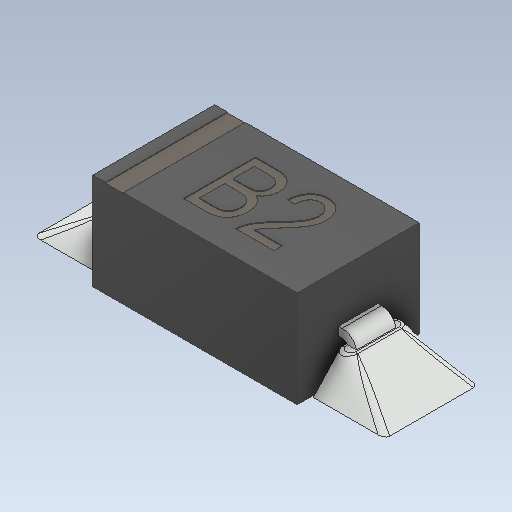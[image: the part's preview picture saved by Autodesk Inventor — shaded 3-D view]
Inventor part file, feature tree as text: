
AUTODESK INVENTOR PART (.ipt)
format: ipt  version: 2020 (Build 240168000, 168)  size: 343,040 bytes
history: native  units: in
note: dims shown in document units (in); Inventor stores cm internally (conversion verified against a paired STEP export)
features: fillet x1
ambient origin geometry x8: Origin, YZ Plane, XZ Plane, XY Plane, X Axis, Y Axis, Z Axis, Center Point
bodies: Solid1 (feature_tree)
feature tree (1):
  fillet  "Fillet9"  [1 undecoded]
note: 1 required parameter value undecoded (feature->parameter linkage not recoverable at this tier; creation-order binding heuristic only, values carry confidence <= 0.55)
